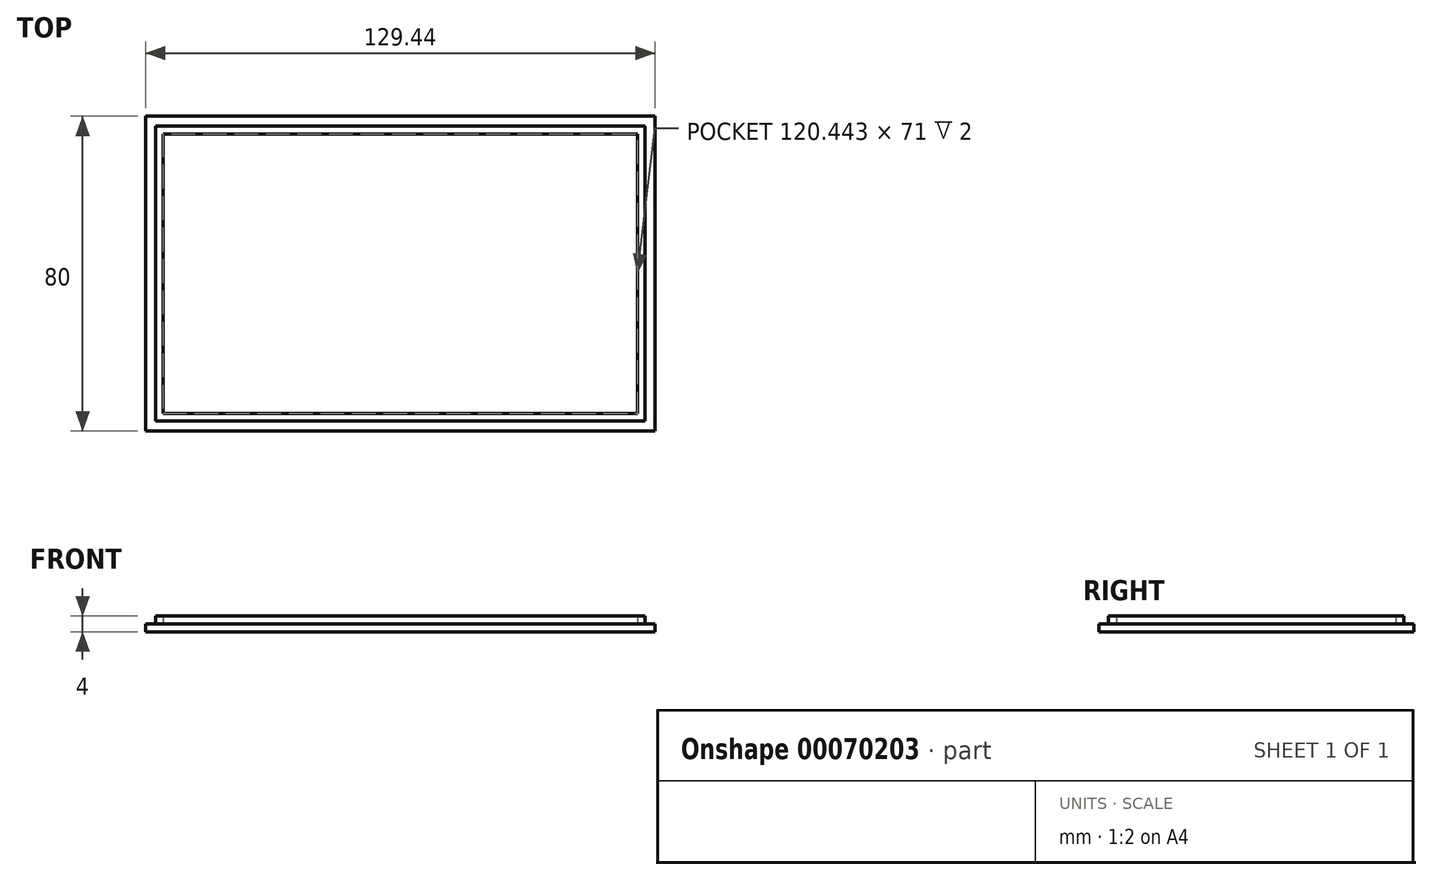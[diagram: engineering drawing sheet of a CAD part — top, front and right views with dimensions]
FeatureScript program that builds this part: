
annotation { "Feature Type Name" : "Feature", "Feature Type Description" : "" }
export const myFeature = defineFeature(function(context is Context, id is Id, definition is map)
    precondition{}
    {
        {
            var Q0;
            Q0=qCreatedBy(makeId("Top.planeOp"),FACE);
            var sketch = newSketch(context, id + "F0", { "sketchPlane" : qUnion([Q0])});
            skLineSegment(sketch, "E0.rect.bottom", {"start": v(-64.72, 40) * mm, "end": v(64.72, 40) * mm});
            skLineSegment(sketch, "E0.rect.top", {"start": v(-64.72, -40) * mm, "end": v(64.72, -40) * mm});
            skLineSegment(sketch, "E0.rect.left", {"start": v(-64.72, 40) * mm, "end": v(-64.72, -40) * mm});
            skLineSegment(sketch, "E0.rect.right", {"start": v(64.72, 40) * mm, "end": v(64.72, -40) * mm});
            skPoint(sketch, "E0.rect.middle", {"position": v(0, 0) * mm});
            skSolve(sketch);
        }
        {
            var Q0;
            Q0=qSketchRegion(id+"F0",true);
            extrude(context, id + "F1", {"entities" : qUnion([Q0]), "oppositeDirection" : true, "depth" : 2 * mm});
        }
        {
            var Q0;
            Q0=qCreatedBy(makeId("Top.planeOp"),FACE);
            var sketch = newSketch(context, id + "F2", { "sketchPlane" : qUnion([Q0])});
            skLineSegment(sketch, "E1.rect.bottom", {"start": v(62.22, 37.5) * mm, "end": v(-62.22, 37.5) * mm});
            skLineSegment(sketch, "E1.rect.top", {"start": v(62.22, -37.5) * mm, "end": v(-62.22, -37.5) * mm});
            skLineSegment(sketch, "E1.rect.left", {"start": v(62.22, 37.5) * mm, "end": v(62.22, -37.5) * mm});
            skLineSegment(sketch, "E1.rect.right", {"start": v(-62.22, 37.5) * mm, "end": v(-62.22, -37.5) * mm});
            skPoint(sketch, "E1.rect.middle", {"position": v(0, 0) * mm});
            skLineSegment(sketch, "E2.0", {"start": v(60.22, 35.5) * mm, "end": v(-60.22, 35.5) * mm});
            skLineSegment(sketch, "E2.1", {"start": v(60.22, 35.5) * mm, "end": v(60.22, -35.5) * mm});
            skLineSegment(sketch, "E2.2", {"start": v(60.22, -35.5) * mm, "end": v(-60.22, -35.5) * mm});
            skLineSegment(sketch, "E2.3", {"start": v(-60.22, 35.5) * mm, "end": v(-60.22, -35.5) * mm});
            skSolve(sketch);
        }
        {
            var Q0;
            Q0 = qSketchRegion(id + "F2", true);
            extrude(context, id + "F3", {"entities" : qUnion([Q0]), "operationType" : NewBodyOperationType.ADD, "depth" : 2 * mm});
        }
    });
